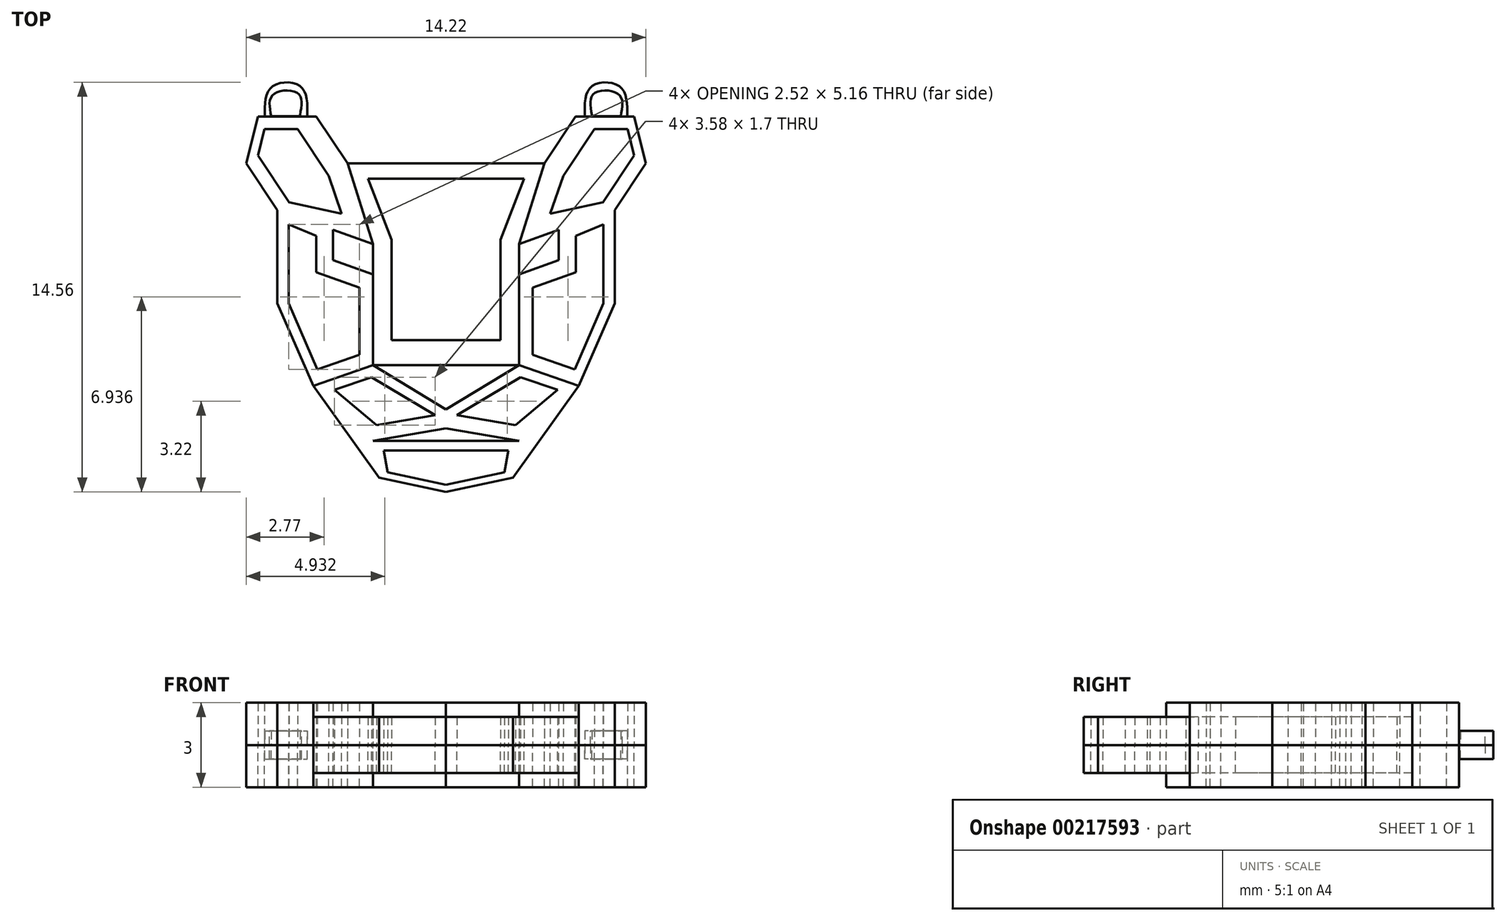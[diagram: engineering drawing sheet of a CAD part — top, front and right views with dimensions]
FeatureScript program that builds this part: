
annotation { "Feature Type Name" : "Feature", "Feature Type Description" : "" }
export const myFeature = defineFeature(function(context is Context, id is Id, definition is map)
    precondition{}
    {
        {
            var Q0;
            Q0=qCreatedBy(makeId("Top.planeOp"),FACE);
            var sketch = newSketch(context, id + "F0", { "sketchPlane" : qUnion([Q0])});
            skLineSegment(sketch, "E0", {"start": v(0, 0) * mm, "end": v(3.5, 0) * mm});
            skLineSegment(sketch, "E1", {"start": v(3.5, 0) * mm, "end": v(6, -1.66) * mm});
            skLineSegment(sketch, "E2", {"start": v(3.5, 0) * mm, "end": v(2.6, -2.86) * mm});
            skLineSegment(sketch, "E3", {"start": v(2.6, -2.86) * mm, "end": v(6, -1.66) * mm});
            skLineSegment(sketch, "E4", {"start": v(3.5, 0) * mm, "end": v(4.6, 1.66) * mm});
            skLineSegment(sketch, "E5", {"start": v(6, -1.66) * mm, "end": v(7.1, 0) * mm});
            skLineSegment(sketch, "E6", {"start": v(7.1, 0) * mm, "end": v(4.6, 1.66) * mm});
            skLineSegment(sketch, "E7", {"start": v(6.7, 1.66) * mm, "end": v(4.6, 1.66) * mm});
            skLineSegment(sketch, "E8", {"start": v(6, -1.66) * mm, "end": v(6, -4.97) * mm});
            skLineSegment(sketch, "E9", {"start": v(2.6, -2.86) * mm, "end": v(2.6, -7.18) * mm});
            skLineSegment(sketch, "E10", {"start": v(2.6, -7.18) * mm, "end": v(0, -7.18) * mm});
            skLineSegment(sketch, "E11", {"start": v(2.6, -7.18) * mm, "end": v(0, -8.74) * mm});
            skLineSegment(sketch, "E12", {"start": v(0, -8.74) * mm, "end": v(0, -9.42) * mm});
            skLineSegment(sketch, "E13", {"start": v(0, -9.42) * mm, "end": v(2.6, -9.86) * mm});
            skLineSegment(sketch, "E14", {"start": v(2.6, -9.86) * mm, "end": v(0, -9.86) * mm});
            skLineSegment(sketch, "E15", {"start": v(2.6, -9.86) * mm, "end": v(2.38, -11.18) * mm});
            skLineSegment(sketch, "E16", {"start": v(2.38, -11.18) * mm, "end": v(0, -11.68) * mm});
            skLineSegment(sketch, "E17.MirrorCS", {"start": v(0, 0) * mm, "end": v(-3.5, 0) * mm});
            skLineSegment(sketch, "E18.MirrorCS", {"start": v(-3.5, 0) * mm, "end": v(-4.6, 1.66) * mm});
            skLineSegment(sketch, "E19.MirrorCS", {"start": v(-7.1, 0) * mm, "end": v(-4.6, 1.66) * mm});
            skLineSegment(sketch, "E20.MirrorCS", {"start": v(-3.5, 0) * mm, "end": v(-6, -1.66) * mm});
            skLineSegment(sketch, "E21.MirrorCS", {"start": v(-3.5, 0) * mm, "end": v(-2.6, -2.86) * mm});
            skLineSegment(sketch, "E22.MirrorCS", {"start": v(-2.6, -2.86) * mm, "end": v(-6, -1.66) * mm});
            skLineSegment(sketch, "E23.MirrorCS", {"start": v(-6, -1.66) * mm, "end": v(-7.1, 0) * mm});
            skLineSegment(sketch, "E24.MirrorCS", {"start": v(-6, -1.66) * mm, "end": v(-6, -4.97) * mm});
            skLineSegment(sketch, "E25.MirrorCS", {"start": v(-2.6, -2.86) * mm, "end": v(-2.6, -7.18) * mm});
            skLineSegment(sketch, "E26.MirrorCS", {"start": v(-2.6, -7.18) * mm, "end": v(0, -7.18) * mm});
            skLineSegment(sketch, "E27.MirrorCS", {"start": v(-2.6, -7.18) * mm, "end": v(0, -8.74) * mm});
            skLineSegment(sketch, "E28.MirrorCS", {"start": v(0, -9.42) * mm, "end": v(-2.6, -9.86) * mm});
            skLineSegment(sketch, "E29.MirrorCS", {"start": v(-2.6, -9.86) * mm, "end": v(0, -9.86) * mm});
            skLineSegment(sketch, "E30.MirrorCS", {"start": v(-2.38, -11.18) * mm, "end": v(0, -11.68) * mm});
            skLineSegment(sketch, "E31", {"start": v(-2.6, -7.18) * mm, "end": v(-4.72, -7.9) * mm});
            skLineSegment(sketch, "E32", {"start": v(-4.72, -7.9) * mm, "end": v(-2.38, -11.18) * mm});
            skLineSegment(sketch, "E33", {"start": v(-6, -4.97) * mm, "end": v(-4.72, -7.9) * mm});
            skLineSegment(sketch, "E34", {"start": v(-2.6, -9.86) * mm, "end": v(-4.72, -7.9) * mm});
            skLineSegment(sketch, "E35.MirrorCS", {"start": v(4.72, -7.9) * mm, "end": v(2.38, -11.18) * mm});
            skLineSegment(sketch, "E36.MirrorCS", {"start": v(2.6, -9.86) * mm, "end": v(4.72, -7.9) * mm});
            skLineSegment(sketch, "E37.MirrorCS", {"start": v(6, -4.97) * mm, "end": v(4.72, -7.9) * mm});
            skLineSegment(sketch, "E38", {"start": v(4.72, -7.9) * mm, "end": v(2.6, -7.18) * mm});
            skLineSegment(sketch, "E39", {"start": v(-2.6, -9.86) * mm, "end": v(-2.38, -11.18) * mm});
            skLineSegment(sketch, "E40", {"start": v(-4.01, -2.36) * mm, "end": v(-4.01, -3.44) * mm});
            skLineSegment(sketch, "E41", {"start": v(-4.01, -3.44) * mm, "end": v(-2.6, -3.94) * mm});
            skLineSegment(sketch, "E42.MirrorCS", {"start": v(4.01, -3.44) * mm, "end": v(2.6, -3.94) * mm});
            skLineSegment(sketch, "E43.MirrorCS", {"start": v(4.01, -2.36) * mm, "end": v(4.01, -3.44) * mm});
            skLineSegment(sketch, "E44", {"start": v(7.1, 0) * mm, "end": v(6.7, 1.66) * mm});
            skLineSegment(sketch, "E45.MirrorCS", {"start": v(-7.1, 0) * mm, "end": v(-6.7, 1.66) * mm});
            skLineSegment(sketch, "E46.MirrorCS", {"start": v(-6.7, 1.66) * mm, "end": v(-4.6, 1.66) * mm});
            skLineSegment(sketch, "E47", {"start": v(-6.46, 1.22) * mm, "end": v(-6.7, 0.28) * mm});
            skLineSegment(sketch, "E48", {"start": v(-6.46, 1.22) * mm, "end": v(-5.28, 1.22) * mm});
            skLineSegment(sketch, "E49", {"start": v(-5.28, 1.22) * mm, "end": v(-4.17, -0.45) * mm});
            skLineSegment(sketch, "E50", {"start": v(-4.17, -0.45) * mm, "end": v(-3.7, -1.79) * mm});
            skLineSegment(sketch, "E51", {"start": v(-6.7, 0.28) * mm, "end": v(-5.58, -1.39) * mm});
            skLineSegment(sketch, "E52", {"start": v(-5.58, -1.39) * mm, "end": v(-3.7, -1.79) * mm});
            skLineSegment(sketch, "E53.MirrorCS", {"start": v(6.46, 1.22) * mm, "end": v(6.7, 0.28) * mm});
            skLineSegment(sketch, "E54.MirrorCS", {"start": v(6.46, 1.22) * mm, "end": v(5.28, 1.22) * mm});
            skLineSegment(sketch, "E55.MirrorCS", {"start": v(5.28, 1.22) * mm, "end": v(4.17, -0.45) * mm});
            skLineSegment(sketch, "E56.MirrorCS", {"start": v(4.17, -0.45) * mm, "end": v(3.7, -1.79) * mm});
            skLineSegment(sketch, "E57.MirrorCS", {"start": v(5.58, -1.39) * mm, "end": v(3.7, -1.79) * mm});
            skLineSegment(sketch, "E58.MirrorCS", {"start": v(6.7, 0.28) * mm, "end": v(5.58, -1.39) * mm});
            skLineSegment(sketch, "E59", {"start": v(-2.77, -0.54) * mm, "end": v(-1.94, -2.72) * mm});
            skLineSegment(sketch, "E60", {"start": v(-1.94, -2.72) * mm, "end": v(-1.94, -6.29) * mm});
            skLineSegment(sketch, "E61", {"start": v(-1.94, -6.29) * mm, "end": v(0, -6.29) * mm});
            skLineSegment(sketch, "E62", {"start": v(-5.6, -2.17) * mm, "end": v(-5.6, -4.97) * mm});
            skLineSegment(sketch, "E63", {"start": v(-5.6, -4.97) * mm, "end": v(-4.58, -7.32) * mm});
            skLineSegment(sketch, "E64", {"start": v(-4.58, -7.32) * mm, "end": v(-3.08, -6.8) * mm});
            skLineSegment(sketch, "E65", {"start": v(-3.08, -6.8) * mm, "end": v(-3.08, -4.41) * mm});
            skLineSegment(sketch, "E66", {"start": v(-3.08, -4.41) * mm, "end": v(-4.01, -4.08) * mm});
            skLineSegment(sketch, "E67", {"start": v(-4.01, -4.08) * mm, "end": v(-4.61, -3.87) * mm});
            skLineSegment(sketch, "E68", {"start": v(-4.61, -3.87) * mm, "end": v(-4.61, -2.57) * mm});
            skLineSegment(sketch, "E69", {"start": v(-4.61, -2.57) * mm, "end": v(-5.6, -2.17) * mm});
            skLineSegment(sketch, "E70.MirrorCS", {"start": v(3.08, -6.8) * mm, "end": v(3.08, -4.41) * mm});
            skLineSegment(sketch, "E71.MirrorCS", {"start": v(3.08, -4.41) * mm, "end": v(4.01, -4.08) * mm});
            skLineSegment(sketch, "E72.MirrorCS", {"start": v(4.01, -4.08) * mm, "end": v(4.61, -3.87) * mm});
            skLineSegment(sketch, "E73.MirrorCS", {"start": v(4.61, -3.87) * mm, "end": v(4.61, -2.57) * mm});
            skLineSegment(sketch, "E74.MirrorCS", {"start": v(4.61, -2.57) * mm, "end": v(5.6, -2.17) * mm});
            skLineSegment(sketch, "E75.MirrorCS", {"start": v(5.6, -2.17) * mm, "end": v(5.6, -4.97) * mm});
            skLineSegment(sketch, "E76.MirrorCS", {"start": v(5.6, -4.97) * mm, "end": v(4.58, -7.32) * mm});
            skLineSegment(sketch, "E77.MirrorCS", {"start": v(4.58, -7.32) * mm, "end": v(3.08, -6.8) * mm});
            skLineSegment(sketch, "E78.MirrorCS", {"start": v(1.94, -6.29) * mm, "end": v(0, -6.29) * mm});
            skLineSegment(sketch, "E79.MirrorCS", {"start": v(1.94, -2.72) * mm, "end": v(1.94, -6.29) * mm});
            skLineSegment(sketch, "E80.MirrorCS", {"start": v(2.77, -0.54) * mm, "end": v(1.94, -2.72) * mm});
            skLineSegment(sketch, "E81", {"start": v(-2.77, -0.54) * mm, "end": v(2.77, -0.54) * mm});
            skLineSegment(sketch, "E82", {"start": v(-3.97, -8.05) * mm, "end": v(-2.65, -7.6) * mm});
            skLineSegment(sketch, "E83", {"start": v(-2.65, -7.6) * mm, "end": v(-0.39, -8.96) * mm});
            skLineSegment(sketch, "E84", {"start": v(-0.39, -8.96) * mm, "end": v(-2.47, -9.31) * mm});
            skLineSegment(sketch, "E85", {"start": v(-2.47, -9.31) * mm, "end": v(-3.97, -8.05) * mm});
            skLineSegment(sketch, "E86", {"start": v(-2.21, -10.2) * mm, "end": v(-2.08, -10.99) * mm});
            skLineSegment(sketch, "E87", {"start": v(-2.08, -10.99) * mm, "end": v(0, -11.43) * mm});
            skLineSegment(sketch, "E88", {"start": v(-2.21, -10.2) * mm, "end": v(0, -10.2) * mm});
            skLineSegment(sketch, "E89.MirrorCS", {"start": v(2.65, -7.6) * mm, "end": v(0.39, -8.96) * mm});
            skLineSegment(sketch, "E90.MirrorCS", {"start": v(3.97, -8.05) * mm, "end": v(2.65, -7.6) * mm});
            skLineSegment(sketch, "E91.MirrorCS", {"start": v(2.47, -9.31) * mm, "end": v(3.97, -8.05) * mm});
            skLineSegment(sketch, "E92.MirrorCS", {"start": v(0.39, -8.96) * mm, "end": v(2.47, -9.31) * mm});
            skLineSegment(sketch, "E93.MirrorCS", {"start": v(2.21, -10.2) * mm, "end": v(2.08, -10.99) * mm});
            skLineSegment(sketch, "E94.MirrorCS", {"start": v(2.08, -10.99) * mm, "end": v(0, -11.43) * mm});
            skLineSegment(sketch, "E95.MirrorCS", {"start": v(2.21, -10.2) * mm, "end": v(0, -10.2) * mm});
            skFitSpline(sketch, "E96", {"points": [v(-6.45, 1.66) * mm, v(-6.19, 2.72) * mm, v(-5.18, 2.74) * mm, v(-4.93, 1.66) * mm], "startDerivative": vector(-0.03, 3.77) * mm, "endDerivative": vector(-0.08, -3.83) * mm});
            skFitSpline(sketch, "E97.MirrorCS", {"points": [v(6.45, 1.66) * mm, v(6.19, 2.72) * mm, v(5.18, 2.74) * mm, v(4.93, 1.66) * mm], "startDerivative": vector(0.03, 3.77) * mm, "endDerivative": vector(0.08, -3.83) * mm});
            skSolve(sketch);
        }
        {
            var Q0;
            {var subQ1=sQuery(id+"F0.wireOp",EDGE,"E2");Q0=makeQuery(id+"F0.imprint","IMPRINT",FACE,{"disambiguationData":[TD([[makeQuery(id+"F0.imprint","IMPRINT",EDGE,{"derivedFrom":subQ1}),1.0]])]});}
            var Q1;
            {var subQ0=sQuery(id+"F0.wireOp",EDGE,"E7");Q1=makeQuery(id+"F0.imprint","IMPRINT",FACE,{"disambiguationData":[TD([[makeQuery(id+"F0.imprint","IMPRINT",EDGE,{"derivedFrom":subQ0}),1.0]])]});}
            var Q2;
            {var subQ0=sQuery(id+"F0.wireOp",EDGE,"E5");Q2=makeQuery(id+"F0.imprint","IMPRINT",FACE,{"disambiguationData":[TD([[makeQuery(id+"F0.imprint","IMPRINT",EDGE,{"derivedFrom":subQ0}),1.0]])]});}
            var Q3;
            {var subQ3=sQuery(id+"F0.wireOp",EDGE,"E8");Q3=makeQuery(id+"F0.imprint","IMPRINT",FACE,{"disambiguationData":[TD([[makeQuery(id+"F0.imprint","IMPRINT",EDGE,{"derivedFrom":subQ3}),-1.0]])]});}
            var Q4;
            {var subQ1=sQuery(id+"F0.wireOp",EDGE,"E21.MirrorCS");Q4=makeQuery(id+"F0.imprint","IMPRINT",FACE,{"disambiguationData":[TD([[makeQuery(id+"F0.imprint","IMPRINT",EDGE,{"derivedFrom":subQ1}),-1.0]])]});}
            var Q5;
            {var subQ3=sQuery(id+"F0.wireOp",EDGE,"E45.MirrorCS");Q5=makeQuery(id+"F0.imprint","IMPRINT",FACE,{"disambiguationData":[TD([[makeQuery(id+"F0.imprint","IMPRINT",EDGE,{"derivedFrom":subQ3}),-1.0]])]});}
            var Q6;
            {var subQ2=sQuery(id+"F0.wireOp",EDGE,"E24.MirrorCS");Q6=makeQuery(id+"F0.imprint","IMPRINT",FACE,{"disambiguationData":[TD([[makeQuery(id+"F0.imprint","IMPRINT",EDGE,{"derivedFrom":subQ2}),1.0]])]});}
            var Q7;
            {var subQ0=sQuery(id+"F0.wireOp",EDGE,"E23.MirrorCS");Q7=makeQuery(id+"F0.imprint","IMPRINT",FACE,{"disambiguationData":[TD([[makeQuery(id+"F0.imprint","IMPRINT",EDGE,{"derivedFrom":subQ0}),-1.0]])]});}
            var Q8;
            {var subQ0=sQuery(id+"F0.wireOp",EDGE,"E18.MirrorCS");Q8=makeQuery(id+"F0.imprint","IMPRINT",FACE,{"disambiguationData":[TD([[makeQuery(id+"F0.imprint","IMPRINT",EDGE,{"derivedFrom":subQ0}),1.0]])]});}
            var Q9;
            Q9=makeQuery(id+"F0.imprint","IMPRINT",FACE,{"disambiguationData":[TD([[makeQuery(id+"F0.imprint","IMPRINT",EDGE,{"derivedFrom":sQuery(id+"F0.wireOp",EDGE,"E10")}),1.0]])]});
            var Q10;
            {var subQ0=sQuery(id+"F0.wireOp",EDGE,"E4");Q10=makeQuery(id+"F0.imprint","IMPRINT",FACE,{"disambiguationData":[TD([[makeQuery(id+"F0.imprint","IMPRINT",EDGE,{"derivedFrom":subQ0}),-1.0]])]});}
            extrude(context, id + "F1", {"entities" : qUnion([Q0, Q1, Q2, Q3, Q4, Q5, Q6, Q7, Q8, Q9, Q10]), "depth" : 1.5 * mm});
        }
        {
            var Q0;
            Q0=makeQuery(id+"F0.imprint","IMPRINT",FACE,{"disambiguationData":[TD([[makeQuery(id+"F0.imprint","IMPRINT",EDGE,{"derivedFrom":sQuery(id+"F0.wireOp",EDGE,"E0")}),-1.0]])]});
            var Q1;
            Q1=makeQuery(id+"F0.imprint","IMPRINT",FACE,{"disambiguationData":[TD([[makeQuery(id+"F0.imprint","IMPRINT",EDGE,{"derivedFrom":sQuery(id+"F0.wireOp",EDGE,"E12")}),-1.0]])]});
            var Q2;
            Q2=makeQuery(id+"F0.imprint","IMPRINT",FACE,{"disambiguationData":[TD([[makeQuery(id+"F0.imprint","IMPRINT",EDGE,{"derivedFrom":sQuery(id+"F0.wireOp",EDGE,"E32")}),1.0]])]});
            var Q3;
            Q3=makeQuery(id+"F0.imprint","IMPRINT",FACE,{"disambiguationData":[TD([[makeQuery(id+"F0.imprint","IMPRINT",EDGE,{"derivedFrom":sQuery(id+"F0.wireOp",EDGE,"E14")}),1.0]])]});
            var Q4;
            Q4=makeQuery(id+"F0.imprint","IMPRINT",FACE,{"disambiguationData":[TD([[makeQuery(id+"F0.imprint","IMPRINT",EDGE,{"derivedFrom":sQuery(id+"F0.wireOp",EDGE,"E15")}),1.0]])]});
            var Q5;
            Q5=makeQuery(id+"F0.imprint","IMPRINT",FACE,{"disambiguationData":[TD([[makeQuery(id+"F0.imprint","IMPRINT",EDGE,{"derivedFrom":sQuery(id+"F0.wireOp",EDGE,"E11")}),1.0]])]});
            extrude(context, id + "F2", {"entities" : qUnion([Q0, Q1, Q2, Q3, Q4, Q5]), "depth" : 1 * mm});
        }
        {
            var Q0;
            Q0=qCreatedBy(makeId("Top.planeOp"),FACE);
            var sketch = newSketch(context, id + "F3", { "sketchPlane" : qUnion([Q0])});
            skFitSpline(sketch, "E98", {"points": [v(-6.21, 1.68) * mm, v(-6.15, 2.44) * mm, v(-5.26, 2.5) * mm, v(-5.2, 1.72) * mm], "startDerivative": vector(-0.57, 2.76) * mm, "endDerivative": vector(-0.53, -2.87) * mm});
            skLineSegment(sketch, "E99", {"start": v(-6.21, 1.68) * mm, "end": v(-5.2, 1.68) * mm});
            skLineSegment(sketch, "E100", {"start": v(-5.2, 1.68) * mm, "end": v(-5.2, 1.72) * mm});
            skFitSpline(sketch, "E101.MirrorCS", {"points": [v(6.21, 1.68) * mm, v(6.15, 2.44) * mm, v(5.26, 2.5) * mm, v(5.2, 1.72) * mm], "startDerivative": vector(0.57, 2.76) * mm, "endDerivative": vector(0.53, -2.87) * mm});
            skLineSegment(sketch, "E102.MirrorCS", {"start": v(6.21, 1.68) * mm, "end": v(5.2, 1.68) * mm});
            skLineSegment(sketch, "E103", {"start": v(5.2, 1.72) * mm, "end": v(5.2, 1.68) * mm});
            skSolve(sketch);
        }
        {
            var Q0;
            {var subQ0=sQuery(id+"F0.wireOp",EDGE,"E96");Q0=makeQuery(id+"F0.imprint","IMPRINT",FACE,{"disambiguationData":[TD([[makeQuery(id+"F0.imprint","IMPRINT",EDGE,{"derivedFrom":subQ0}),-1.0]])]});}
            var Q1;
            {var subQ0=sQuery(id+"F0.wireOp",EDGE,"E97.MirrorCS");Q1=makeQuery(id+"F0.imprint","IMPRINT",FACE,{"disambiguationData":[TD([[makeQuery(id+"F0.imprint","IMPRINT",EDGE,{"derivedFrom":subQ0}),1.0]])]});}
            var Q2;
            Q2=sQuery(id+"F0.wireOp",EDGE,"E96");
            var Q3;
            Q3=sQuery(id+"F0.wireOp",EDGE,"E97.MirrorCS");
            extrude(context, id + "F4", {"entities" : qUnion([Q0, Q1]), "surfaceEntities" : qUnion([Q2, Q3]), "depth" : 0.5 * mm});
        }
        {
            var Q0;
            Q0 = qSketchRegion(id + "F3", true);
            extrude(context, id + "F5", {"entities" : qUnion([Q0]), "operationType" : NewBodyOperationType.REMOVE, "endBound" : BoundingType.THROUGH_ALL, "depth" : 25 * mm});
        }
        {
            var Q0;
            Q0=makeQuery(id+"F1.opExtrude","SWEPT_BODY",BODY,{"disambiguationData":[OSD([sQuery(id+"F0.wireOp",EDGE,"E18.MirrorCS"),sQuery(id+"F0.wireOp",EDGE,"E21.MirrorCS"),sQuery(id+"F0.wireOp",EDGE,"E22.MirrorCS"),sQuery(id+"F0.wireOp",EDGE,"E23.MirrorCS"),sQuery(id+"F0.wireOp",EDGE,"E24.MirrorCS"),sQuery(id+"F0.wireOp",EDGE,"E25.MirrorCS"),sQuery(id+"F0.wireOp",EDGE,"E31"),sQuery(id+"F0.wireOp",EDGE,"E33"),sQuery(id+"F0.wireOp",EDGE,"E40"),sQuery(id+"F0.wireOp",EDGE,"E41"),sQuery(id+"F0.wireOp",EDGE,"E45.MirrorCS"),sQuery(id+"F0.wireOp",EDGE,"E46.MirrorCS"),sQuery(id+"F0.wireOp",EDGE,"E47"),sQuery(id+"F0.wireOp",EDGE,"E48"),sQuery(id+"F0.wireOp",EDGE,"E49"),sQuery(id+"F0.wireOp",EDGE,"E50"),sQuery(id+"F0.wireOp",EDGE,"E51"),sQuery(id+"F0.wireOp",EDGE,"E52"),sQuery(id+"F0.wireOp",EDGE,"E62"),sQuery(id+"F0.wireOp",EDGE,"E63"),sQuery(id+"F0.wireOp",EDGE,"E64"),sQuery(id+"F0.wireOp",EDGE,"E65"),sQuery(id+"F0.wireOp",EDGE,"E66"),sQuery(id+"F0.wireOp",EDGE,"E67"),sQuery(id+"F0.wireOp",EDGE,"E68"),sQuery(id+"F0.wireOp",EDGE,"E69"),sQuery(id+"F0.wireOp",EDGE,"E96")])]});
            var Q1;
            Q1=makeQuery(id+"F2.opExtrude","SWEPT_BODY",BODY,{"disambiguationData":[OSD([sQuery(id+"F0.wireOp",EDGE,"E0"),sQuery(id+"F0.wireOp",EDGE,"E2"),sQuery(id+"F0.wireOp",EDGE,"E9"),sQuery(id+"F0.wireOp",EDGE,"E10"),sQuery(id+"F0.wireOp",EDGE,"E17.MirrorCS"),sQuery(id+"F0.wireOp",EDGE,"E21.MirrorCS"),sQuery(id+"F0.wireOp",EDGE,"E25.MirrorCS"),sQuery(id+"F0.wireOp",EDGE,"E26.MirrorCS"),sQuery(id+"F0.wireOp",EDGE,"E59"),sQuery(id+"F0.wireOp",EDGE,"E60"),sQuery(id+"F0.wireOp",EDGE,"E61"),sQuery(id+"F0.wireOp",EDGE,"E78.MirrorCS"),sQuery(id+"F0.wireOp",EDGE,"E79.MirrorCS"),sQuery(id+"F0.wireOp",EDGE,"E80.MirrorCS"),sQuery(id+"F0.wireOp",EDGE,"E81")])]});
            var Q2;
            Q2=makeQuery(id+"F2.opExtrude","SWEPT_BODY",BODY,{"disambiguationData":[OSD([sQuery(id+"F0.wireOp",EDGE,"E11"),sQuery(id+"F0.wireOp",EDGE,"E13"),sQuery(id+"F0.wireOp",EDGE,"E14"),sQuery(id+"F0.wireOp",EDGE,"E16"),sQuery(id+"F0.wireOp",EDGE,"E27.MirrorCS"),sQuery(id+"F0.wireOp",EDGE,"E28.MirrorCS"),sQuery(id+"F0.wireOp",EDGE,"E29.MirrorCS"),sQuery(id+"F0.wireOp",EDGE,"E30.MirrorCS"),sQuery(id+"F0.wireOp",EDGE,"E31"),sQuery(id+"F0.wireOp",EDGE,"E32"),sQuery(id+"F0.wireOp",EDGE,"E35.MirrorCS"),sQuery(id+"F0.wireOp",EDGE,"E38"),sQuery(id+"F0.wireOp",EDGE,"E82"),sQuery(id+"F0.wireOp",EDGE,"E83"),sQuery(id+"F0.wireOp",EDGE,"E84"),sQuery(id+"F0.wireOp",EDGE,"E85"),sQuery(id+"F0.wireOp",EDGE,"E86"),sQuery(id+"F0.wireOp",EDGE,"E87"),sQuery(id+"F0.wireOp",EDGE,"E88"),sQuery(id+"F0.wireOp",EDGE,"E89.MirrorCS"),sQuery(id+"F0.wireOp",EDGE,"E90.MirrorCS"),sQuery(id+"F0.wireOp",EDGE,"E91.MirrorCS"),sQuery(id+"F0.wireOp",EDGE,"E92.MirrorCS"),sQuery(id+"F0.wireOp",EDGE,"E93.MirrorCS"),sQuery(id+"F0.wireOp",EDGE,"E94.MirrorCS"),sQuery(id+"F0.wireOp",EDGE,"E95.MirrorCS")])]});
            var Q3;
            Q3=makeQuery(id+"F1.opExtrude","SWEPT_BODY",BODY,{"disambiguationData":[OSD([sQuery(id+"F0.wireOp",EDGE,"E2"),sQuery(id+"F0.wireOp",EDGE,"E3"),sQuery(id+"F0.wireOp",EDGE,"E4"),sQuery(id+"F0.wireOp",EDGE,"E5"),sQuery(id+"F0.wireOp",EDGE,"E7"),sQuery(id+"F0.wireOp",EDGE,"E8"),sQuery(id+"F0.wireOp",EDGE,"E9"),sQuery(id+"F0.wireOp",EDGE,"E37.MirrorCS"),sQuery(id+"F0.wireOp",EDGE,"E38"),sQuery(id+"F0.wireOp",EDGE,"E42.MirrorCS"),sQuery(id+"F0.wireOp",EDGE,"E43.MirrorCS"),sQuery(id+"F0.wireOp",EDGE,"E44"),sQuery(id+"F0.wireOp",EDGE,"E53.MirrorCS"),sQuery(id+"F0.wireOp",EDGE,"E54.MirrorCS"),sQuery(id+"F0.wireOp",EDGE,"E55.MirrorCS"),sQuery(id+"F0.wireOp",EDGE,"E56.MirrorCS"),sQuery(id+"F0.wireOp",EDGE,"E57.MirrorCS"),sQuery(id+"F0.wireOp",EDGE,"E58.MirrorCS"),sQuery(id+"F0.wireOp",EDGE,"E71.MirrorCS"),sQuery(id+"F0.wireOp",EDGE,"E72.MirrorCS"),sQuery(id+"F0.wireOp",EDGE,"E73.MirrorCS"),sQuery(id+"F0.wireOp",EDGE,"E74.MirrorCS"),sQuery(id+"F0.wireOp",EDGE,"E75.MirrorCS"),sQuery(id+"F0.wireOp",EDGE,"E76.MirrorCS"),sQuery(id+"F0.wireOp",EDGE,"E77.MirrorCS"),sQuery(id+"F0.wireOp",EDGE,"E70.MirrorCS"),sQuery(id+"F0.wireOp",EDGE,"E97.MirrorCS")])]});
            var Q4;
            Q4=makeQuery(id+"F1.opExtrude","SWEPT_BODY",BODY,{"disambiguationData":[OSD([sQuery(id+"F0.wireOp",EDGE,"E10"),sQuery(id+"F0.wireOp",EDGE,"E11"),sQuery(id+"F0.wireOp",EDGE,"E26.MirrorCS"),sQuery(id+"F0.wireOp",EDGE,"E27.MirrorCS")])]});
            var Q5;
            Q5=makeQuery(id+"F4.opExtrude","SWEPT_BODY",BODY,{"disambiguationData":[OSD([sQuery(id+"F0.wireOp",EDGE,"E46.MirrorCS"),sQuery(id+"F0.wireOp",EDGE,"E96")])]});
            var Q6;
            Q6=makeQuery(id+"F4.opExtrude","SWEPT_BODY",BODY,{"disambiguationData":[OSD([sQuery(id+"F0.wireOp",EDGE,"E7"),sQuery(id+"F0.wireOp",EDGE,"E97.MirrorCS")])]});
            var Q7;
            Q7=qCreatedBy(makeId("Top.planeOp"),FACE);
            mirror(context, id + "F6", {"entities" : qUnion([Q0, Q1, Q2, Q3, Q4, Q5, Q6]), "mirrorPlane" : qUnion([Q7])});
        }
    });
